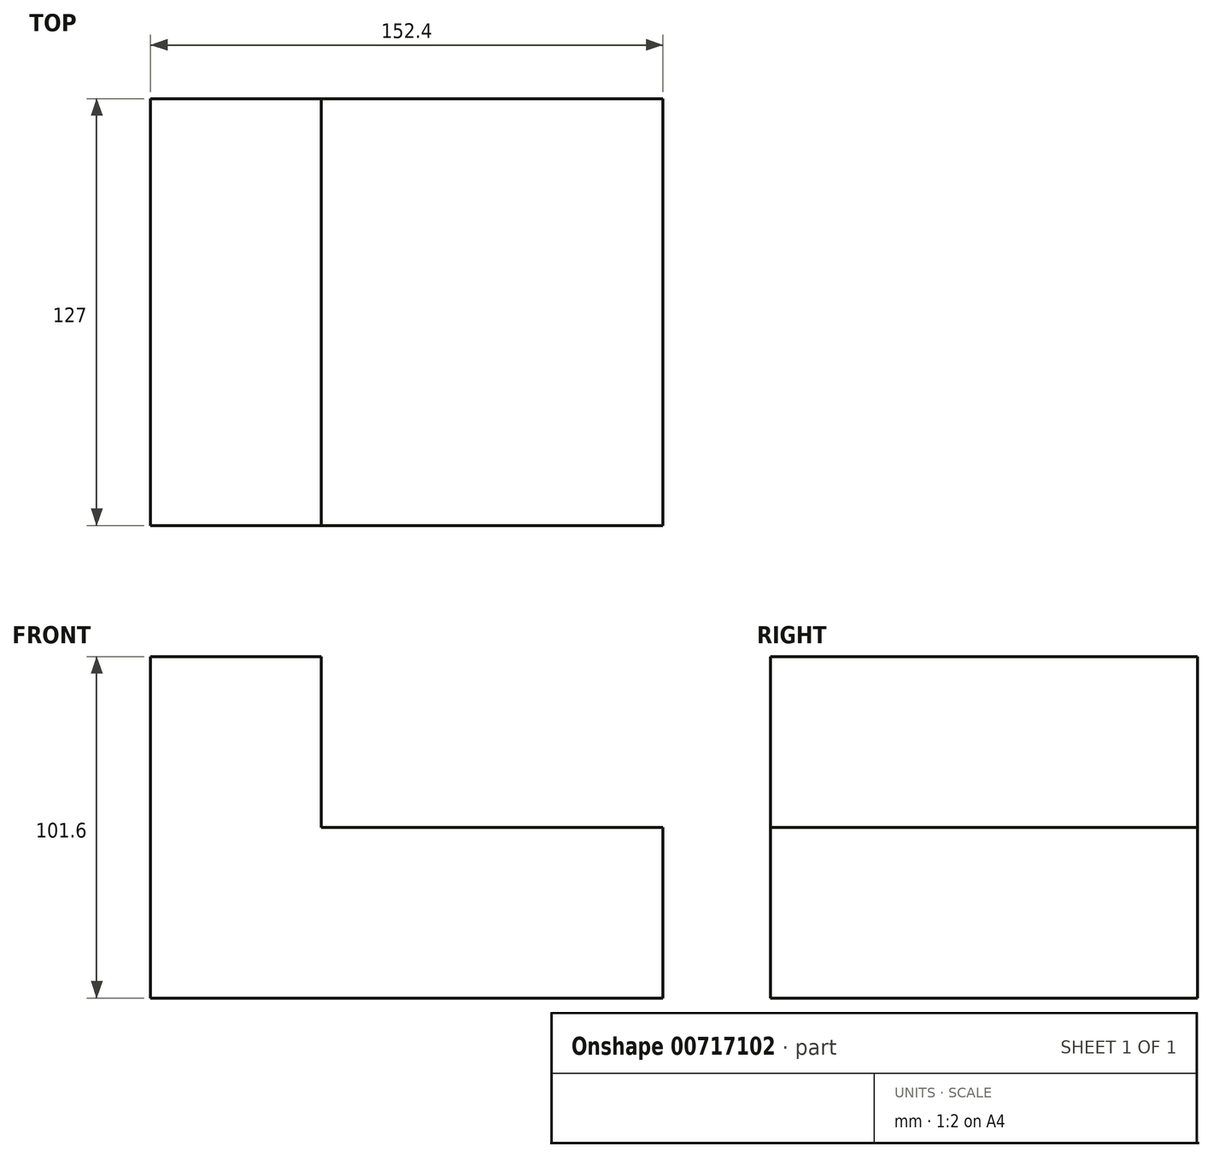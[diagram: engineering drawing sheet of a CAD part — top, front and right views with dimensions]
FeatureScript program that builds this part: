
annotation { "Feature Type Name" : "Feature", "Feature Type Description" : "" }
export const myFeature = defineFeature(function(context is Context, id is Id, definition is map)
    precondition{}
    {
        {
            var Q0;
            Q0=qCreatedBy(makeId("Front.planeOp"),FACE);
            var sketch = newSketch(context, id + "F0", { "sketchPlane" : qUnion([Q0])});
            skLineSegment(sketch, "E0", {"start": v(-119.56, -57.26) * mm, "end": v(32.84, -57.26) * mm});
            skLineSegment(sketch, "E1", {"start": v(32.84, -57.26) * mm, "end": v(32.84, -6.46) * mm});
            skLineSegment(sketch, "E2", {"start": v(32.84, -6.46) * mm, "end": v(-68.76, -6.46) * mm});
            skLineSegment(sketch, "E3", {"start": v(-68.76, -6.46) * mm, "end": v(-68.76, 44.34) * mm});
            skLineSegment(sketch, "E4", {"start": v(-68.76, 44.34) * mm, "end": v(-119.56, 44.34) * mm});
            skLineSegment(sketch, "E5", {"start": v(-119.56, 44.34) * mm, "end": v(-119.56, -57.26) * mm});
            skSolve(sketch);
        }
        {
            var Q0;
            Q0=makeQuery(id+"F0.imprint","IMPRINT",FACE,{"disambiguationData":[TD([[makeQuery(id+"F0.imprint","IMPRINT",EDGE,{"derivedFrom":sQuery(id+"F0.wireOp",EDGE,"E0")}),1.0]])]});
            extrude(context, id + "F1", {"entities" : qUnion([Q0]), "depth" : 127 * mm, "offsetDistance" : 25.4 * mm});
        }
    });
